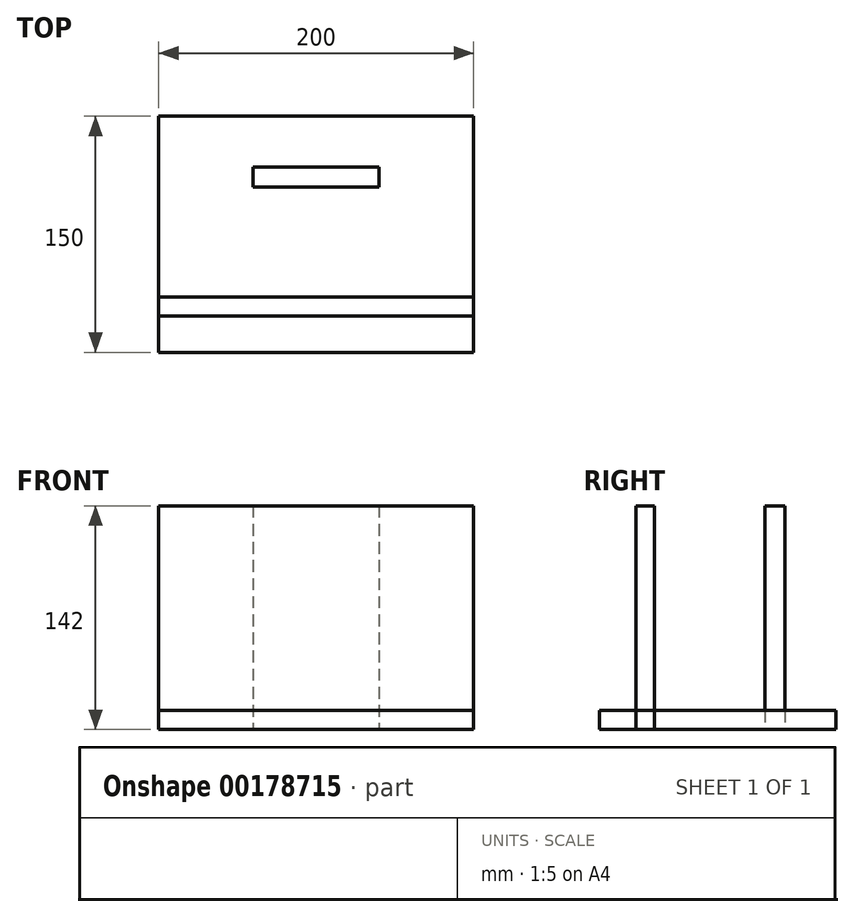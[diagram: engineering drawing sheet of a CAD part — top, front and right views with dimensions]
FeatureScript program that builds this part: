
annotation { "Feature Type Name" : "Feature", "Feature Type Description" : "" }
export const myFeature = defineFeature(function(context is Context, id is Id, definition is map)
    precondition{}
    {
        {
            var Q0;
            Q0=qCreatedBy(makeId("Top.planeOp"),FACE);
            var sketch = newSketch(context, id + "F0", { "sketchPlane" : qUnion([Q0])});
            skLineSegment(sketch, "E0.bottom", {"start": v(100, -75) * mm, "end": v(-100, -75) * mm});
            skLineSegment(sketch, "E0.top", {"start": v(100, 75) * mm, "end": v(-100, 75) * mm});
            skLineSegment(sketch, "E0.left", {"start": v(100, -75) * mm, "end": v(100, 75) * mm});
            skLineSegment(sketch, "E0.right", {"start": v(-100, -75) * mm, "end": v(-100, 75) * mm});
            skPoint(sketch, "E0.middle", {"position": v(0, 0) * mm});
            skSolve(sketch);
        }
        {
            var Q0;
            Q0=makeQuery(id+"F0.imprint","IMPRINT",FACE,{"disambiguationData":[TD([[makeQuery(id+"F0.imprint","IMPRINT",EDGE,{"derivedFrom":sQuery(id+"F0.wireOp",EDGE,"E0.bottom")}),-1.0]])]});
            extrude(context, id + "F1", {"entities" : qUnion([Q0]), "depth" : 12 * mm});
        }
        {
            var Q0;
            Q0=makeQuery(id+"F1.opExtrude","CAP_FACE",FACE,{"disambiguationData":[OSD([sQuery(id+"F0.wireOp",EDGE,"E0.bottom"),sQuery(id+"F0.wireOp",EDGE,"E0.top"),sQuery(id+"F0.wireOp",EDGE,"E0.left"),sQuery(id+"F0.wireOp",EDGE,"E0.right")])],"isStart":true});
            var sketch = newSketch(context, id + "F2", { "sketchPlane" : qUnion([Q0])});
            skLineSegment(sketch, "E1.bottom", {"start": v(100, 52) * mm, "end": v(-100, 52) * mm});
            skLineSegment(sketch, "E1.top", {"start": v(100, 40) * mm, "end": v(-100, 40) * mm});
            skLineSegment(sketch, "E1.left", {"start": v(100, 52) * mm, "end": v(100, 40) * mm});
            skLineSegment(sketch, "E1.right", {"start": v(-100, 52) * mm, "end": v(-100, 40) * mm});
            skLineSegment(sketch, "E2.bottom", {"start": v(40, -30) * mm, "end": v(-40, -30) * mm});
            skLineSegment(sketch, "E2.top", {"start": v(40, -42.6) * mm, "end": v(-40, -42.6) * mm});
            skLineSegment(sketch, "E2.left", {"start": v(40, -30) * mm, "end": v(40, -42.6) * mm});
            skLineSegment(sketch, "E2.right", {"start": v(-40, -30) * mm, "end": v(-40, -42.6) * mm});
            skLineSegment(sketch, "E3", {"start": v(0, 0) * mm, "end": v(0, -30) * mm, "construction": true});
            skSolve(sketch);
        }
        {
            var Q0;
            Q0=qSketchRegion(id+"F2",true);
            extrude(context, id + "F3", {"entities" : qUnion([Q0]), "oppositeDirection" : true, "depth" : 142 * mm});
        }
    });
